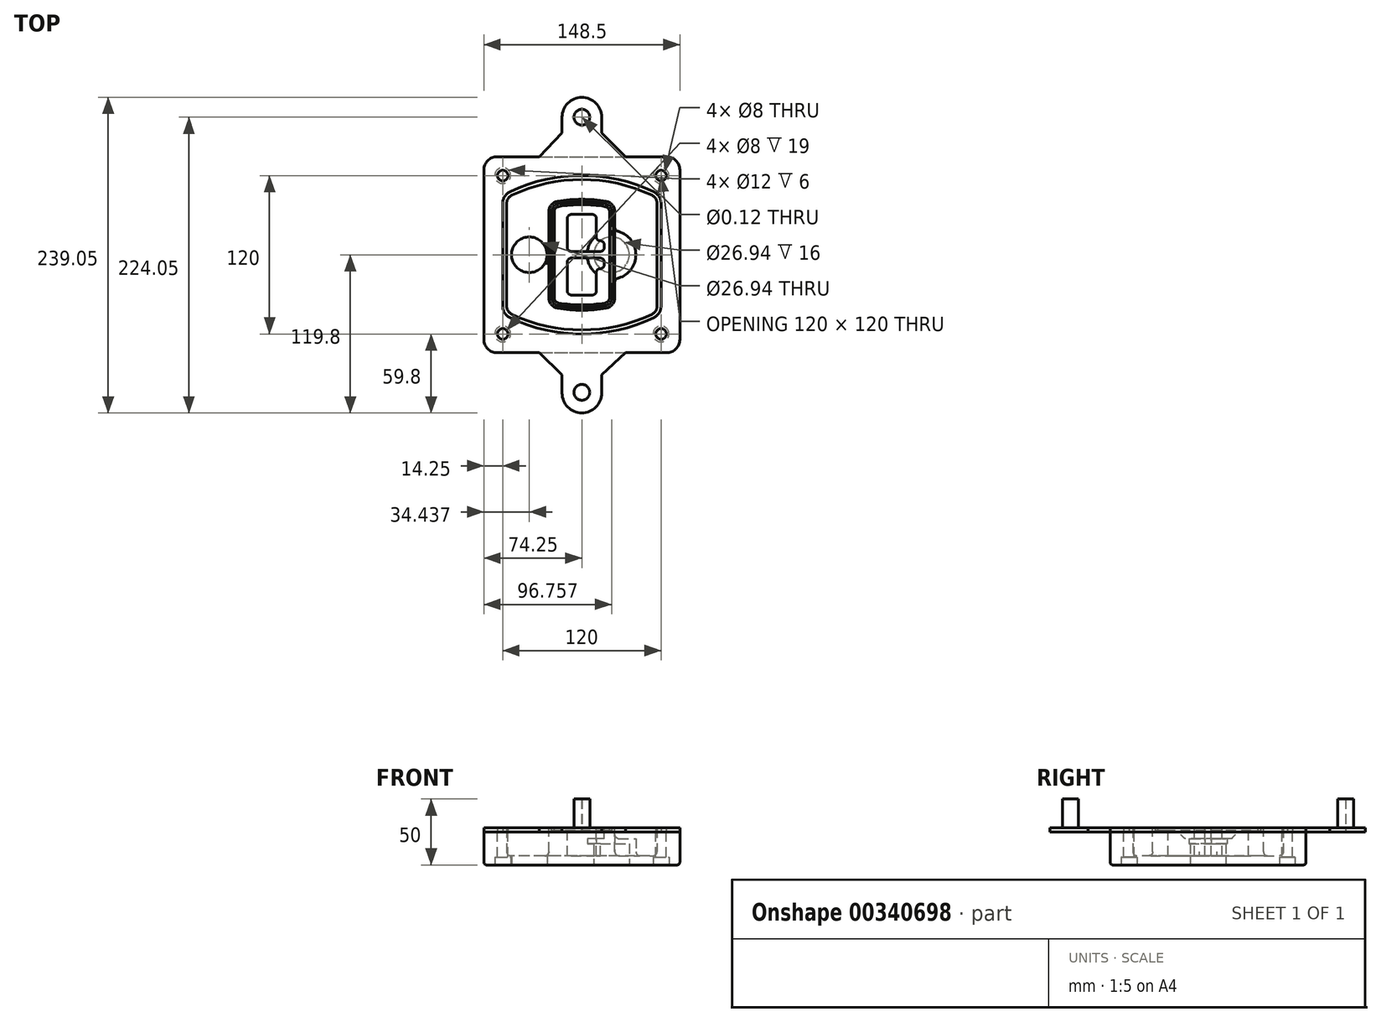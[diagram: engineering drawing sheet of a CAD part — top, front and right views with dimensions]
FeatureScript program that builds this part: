
annotation { "Feature Type Name" : "Feature", "Feature Type Description" : "" }
export const myFeature = defineFeature(function(context is Context, id is Id, definition is map)
    precondition{}
    {
        {
            var Q0;
            Q0=qCreatedBy(makeId("Top.planeOp"),FACE);
            var sketch = newSketch(context, id + "F0", { "sketchPlane" : qUnion([Q0])});
            skPoint(sketch, "E0.rect.middle", {"position": v(0, 0) * mm});
            skLineSegment(sketch, "E1.bottom", {"start": v(-64.25, -74.25) * mm, "end": v(64.25, -74.25) * mm});
            skLineSegment(sketch, "E1.top", {"start": v(-64.25, 74.25) * mm, "end": v(64.25, 74.25) * mm});
            skLineSegment(sketch, "E1.left", {"start": v(-74.25, -64.25) * mm, "end": v(-74.25, 64.25) * mm});
            skLineSegment(sketch, "E1.right", {"start": v(74.25, -64.25) * mm, "end": v(74.25, 64.25) * mm});
            skLineSegment(sketch, "E2", {"start": v(-74.25, 74.25) * mm, "end": v(74.25, -74.25) * mm, "construction": true});
            skLineSegment(sketch, "E3", {"start": v(74.25, 74.25) * mm, "end": v(-74.25, -74.25) * mm, "construction": true});
            skCircle(sketch, "E4", {"center": v(-60, 60) * mm, "radius": 4 * mm});
            skCircle(sketch, "E5", {"center": v(60, 60) * mm, "radius": 4 * mm});
            skCircle(sketch, "E6", {"center": v(60, -60) * mm, "radius": 4 * mm});
            skCircle(sketch, "E7", {"center": v(-60, -60) * mm, "radius": 4 * mm});
            skLineSegment(sketch, "E8", {"start": v(-60, 60) * mm, "end": v(60, 60) * mm, "construction": true});
            skLineSegment(sketch, "E9", {"start": v(60, 60) * mm, "end": v(60, -60) * mm, "construction": true});
            skLineSegment(sketch, "E10", {"start": v(60, -60) * mm, "end": v(-60, -60) * mm, "construction": true});
            skLineSegment(sketch, "E11", {"start": v(-60, -60) * mm, "end": v(-60, 60) * mm, "construction": true});
            skLineSegment(sketch, "E12", {"start": v(-60, 38.83) * mm, "end": v(-60, -38.83) * mm});
            skLineSegment(sketch, "E13", {"start": v(60, 38.83) * mm, "end": v(60, -38.83) * mm});
            skArc(sketch, "E14", {"start": v(54.26, 47.88) * mm, "mid": v(0, 60) * mm, "end": v(-54.26, 47.88) * mm});
            skArc(sketch, "E15", {"start": v(-54.26, -47.88) * mm, "mid": v(0, -60) * mm, "end": v(54.26, -47.88) * mm});
            skLineSegment(sketch, "E16", {"start": v(-60, 0) * mm, "end": v(60, 0) * mm, "construction": true});
            skPoint(sketch, "E17.visualSharp", {"position": v(-60, -45) * mm});
            skArc(sketch, "E17.filletArc", {"start": v(-60, -38.83) * mm, "mid": v(-58.44, -44.2) * mm, "end": v(-54.26, -47.88) * mm});
            skPoint(sketch, "E18.visualSharp", {"position": v(-60, 45) * mm});
            skArc(sketch, "E18.filletArc", {"start": v(-54.26, 47.88) * mm, "mid": v(-58.44, 44.2) * mm, "end": v(-60, 38.83) * mm});
            skPoint(sketch, "E19.visualSharp", {"position": v(60, 45) * mm});
            skArc(sketch, "E19.filletArc", {"start": v(60, 38.83) * mm, "mid": v(58.44, 44.2) * mm, "end": v(54.26, 47.88) * mm});
            skPoint(sketch, "E20.visualSharp", {"position": v(60, -45) * mm});
            skArc(sketch, "E20.filletArc", {"start": v(54.26, -47.88) * mm, "mid": v(58.44, -44.2) * mm, "end": v(60, -38.83) * mm});
            skPoint(sketch, "E21.visualSharp", {"position": v(-74.25, 74.25) * mm});
            skArc(sketch, "E21.filletArc", {"start": v(-64.25, 74.25) * mm, "mid": v(-71.32, 71.32) * mm, "end": v(-74.25, 64.25) * mm});
            skPoint(sketch, "E22.visualSharp", {"position": v(74.25, 74.25) * mm});
            skArc(sketch, "E22.filletArc", {"start": v(74.25, 64.25) * mm, "mid": v(71.32, 71.32) * mm, "end": v(64.25, 74.25) * mm});
            skPoint(sketch, "E23.visualSharp", {"position": v(74.25, -74.25) * mm});
            skArc(sketch, "E23.filletArc", {"start": v(64.25, -74.25) * mm, "mid": v(71.32, -71.32) * mm, "end": v(74.25, -64.25) * mm});
            skPoint(sketch, "E24.visualSharp", {"position": v(-74.25, -74.25) * mm});
            skArc(sketch, "E24.filletArc", {"start": v(-74.25, -64.25) * mm, "mid": v(-71.32, -71.32) * mm, "end": v(-64.25, -74.25) * mm});
            skArc(sketch, "E25.0", {"start": v(57, 38.83) * mm, "mid": v(55.9, 42.58) * mm, "end": v(52.98, 45.17) * mm});
            skLineSegment(sketch, "E25.1", {"start": v(57, 38.83) * mm, "end": v(57, -38.83) * mm});
            skArc(sketch, "E25.2", {"start": v(52.98, -45.17) * mm, "mid": v(55.9, -42.58) * mm, "end": v(57, -38.83) * mm});
            skArc(sketch, "E25.3", {"start": v(-52.98, -45.17) * mm, "mid": v(0, -57) * mm, "end": v(52.98, -45.17) * mm});
            skArc(sketch, "E25.4", {"start": v(-57, -38.83) * mm, "mid": v(-55.9, -42.58) * mm, "end": v(-52.98, -45.17) * mm});
            skArc(sketch, "E25.5", {"start": v(52.98, 45.17) * mm, "mid": v(0, 57) * mm, "end": v(-52.98, 45.17) * mm});
            skLineSegment(sketch, "E25.6", {"start": v(-57, 38.83) * mm, "end": v(-57, -38.83) * mm});
            skArc(sketch, "E25.7", {"start": v(-52.98, 45.17) * mm, "mid": v(-55.9, 42.58) * mm, "end": v(-57, 38.83) * mm});
            skArc(sketch, "E26.0", {"start": v(-55.96, 51.5) * mm, "mid": v(-61.82, 46.33) * mm, "end": v(-64, 38.83) * mm});
            skArc(sketch, "E26.1", {"start": v(55.96, 51.5) * mm, "mid": v(0, 64) * mm, "end": v(-55.96, 51.5) * mm});
            skArc(sketch, "E26.2", {"start": v(64, 38.83) * mm, "mid": v(61.82, 46.33) * mm, "end": v(55.96, 51.5) * mm});
            skLineSegment(sketch, "E26.3", {"start": v(64, 38.83) * mm, "end": v(64, -38.83) * mm});
            skArc(sketch, "E26.4", {"start": v(55.96, -51.5) * mm, "mid": v(61.82, -46.33) * mm, "end": v(64, -38.83) * mm});
            skLineSegment(sketch, "E26.5", {"start": v(-64, 38.83) * mm, "end": v(-64, -38.83) * mm});
            skArc(sketch, "E26.6", {"start": v(-55.96, -51.5) * mm, "mid": v(0, -64) * mm, "end": v(55.96, -51.5) * mm});
            skArc(sketch, "E26.7", {"start": v(-64, -38.83) * mm, "mid": v(-61.82, -46.33) * mm, "end": v(-55.96, -51.5) * mm});
            skSolve(sketch);
        }
        {
            var Q0;
            Q0=makeQuery(id+"F0.imprint","IMPRINT",FACE,{"disambiguationData":[TD([[makeQuery(id+"F0.imprint","IMPRINT",EDGE,{"derivedFrom":sQuery(id+"F0.wireOp",EDGE,"E1.bottom")}),1.0]])]});
            var Q1;
            Q1=makeQuery(id+"F0.imprint","IMPRINT",FACE,{"disambiguationData":[TD([[makeQuery(id+"F0.imprint","IMPRINT",EDGE,{"derivedFrom":sQuery(id+"F0.wireOp",EDGE,"E12")}),1.0]])]});
            var Q2;
            Q2=makeQuery(id+"F0.imprint","IMPRINT",FACE,{"disambiguationData":[TD([[makeQuery(id+"F0.imprint","IMPRINT",EDGE,{"derivedFrom":sQuery(id+"F0.wireOp",EDGE,"E25.0")}),1.0]])]});
            var Q3;
            Q3=makeQuery(id+"F0.imprint","IMPRINT",FACE,{"disambiguationData":[TD([[makeQuery(id+"F0.imprint","IMPRINT",EDGE,{"derivedFrom":sQuery(id+"F0.wireOp",EDGE,"E12")}),-1.0]])]});
            extrude(context, id + "F1", {"entities" : qUnion([Q0, Q1, Q2, Q3]), "oppositeDirection" : true, "depth" : 25 * mm});
        }
        {
            var Q0;
            Q0=makeQuery(id+"F0.imprint","IMPRINT",FACE,{"disambiguationData":[TD([[makeQuery(id+"F0.imprint","IMPRINT",EDGE,{"derivedFrom":sQuery(id+"F0.wireOp",EDGE,"E12")}),1.0]])]});
            extrude(context, id + "F2", {"entities" : qUnion([Q0]), "operationType" : NewBodyOperationType.ADD, "depth" : 3 * mm});
        }
        {
            var Q0;
            Q0=makeQuery(id+"F0.imprint","IMPRINT",FACE,{"disambiguationData":[TD([[makeQuery(id+"F0.imprint","IMPRINT",EDGE,{"derivedFrom":sQuery(id+"F0.wireOp",EDGE,"E25.0")}),1.0]])]});
            extrude(context, id + "F3", {"entities" : qUnion([Q0]), "operationType" : NewBodyOperationType.REMOVE, "oppositeDirection" : true, "depth" : 18 * mm});
        }
        {
            var Q0;
            Q0=makeQuery(id+"F2.opExtrude","CAP_FACE",FACE,{"disambiguationData":[OSD([sQuery(id+"F0.wireOp",EDGE,"E12"),sQuery(id+"F0.wireOp",EDGE,"E13"),sQuery(id+"F0.wireOp",EDGE,"E14"),sQuery(id+"F0.wireOp",EDGE,"E15"),sQuery(id+"F0.wireOp",EDGE,"E17.filletArc"),sQuery(id+"F0.wireOp",EDGE,"E18.filletArc"),sQuery(id+"F0.wireOp",EDGE,"E19.filletArc"),sQuery(id+"F0.wireOp",EDGE,"E20.filletArc"),sQuery(id+"F0.wireOp",EDGE,"E25.0"),sQuery(id+"F0.wireOp",EDGE,"E25.1"),sQuery(id+"F0.wireOp",EDGE,"E25.2"),sQuery(id+"F0.wireOp",EDGE,"E25.3"),sQuery(id+"F0.wireOp",EDGE,"E25.4"),sQuery(id+"F0.wireOp",EDGE,"E25.5"),sQuery(id+"F0.wireOp",EDGE,"E25.6"),sQuery(id+"F0.wireOp",EDGE,"E25.7")])],"isStart":false});
            var sketch = newSketch(context, id + "F4", { "sketchPlane" : qUnion([Q0])});
            skArc(sketch, "E27.0", {"start": v(-18.34, -40.45) * mm, "mid": v(0, -42) * mm, "end": v(18.34, -40.45) * mm});
            skArc(sketch, "E28.0", {"start": v(18.34, 40.45) * mm, "mid": v(0, 42) * mm, "end": v(-18.34, 40.45) * mm});
            skLineSegment(sketch, "E29", {"start": v(-25, 32.57) * mm, "end": v(-25, -32.57) * mm});
            skLineSegment(sketch, "E30", {"start": v(25, 32.57) * mm, "end": v(25, -32.57) * mm});
            skLineSegment(sketch, "E31", {"start": v(-25, 39.1) * mm, "end": v(25, 39.1) * mm, "construction": true});
            skLineSegment(sketch, "E32", {"start": v(-25, -39.1) * mm, "end": v(25, -39.1) * mm, "construction": true});
            skPoint(sketch, "E33.visualSharp", {"position": v(-25, 39.1) * mm});
            skArc(sketch, "E33.filletArc", {"start": v(-18.34, 40.45) * mm, "mid": v(-23.11, 37.73) * mm, "end": v(-25, 32.57) * mm});
            skPoint(sketch, "E34.visualSharp", {"position": v(25, 39.1) * mm});
            skArc(sketch, "E34.filletArc", {"start": v(25, 32.57) * mm, "mid": v(23.11, 37.73) * mm, "end": v(18.34, 40.45) * mm});
            skPoint(sketch, "E35.visualSharp", {"position": v(25, -39.1) * mm});
            skArc(sketch, "E35.filletArc", {"start": v(18.34, -40.45) * mm, "mid": v(23.11, -37.73) * mm, "end": v(25, -32.57) * mm});
            skPoint(sketch, "E36.visualSharp", {"position": v(-25, -39.1) * mm});
            skArc(sketch, "E36.filletArc", {"start": v(-25, -32.57) * mm, "mid": v(-23.11, -37.73) * mm, "end": v(-18.34, -40.45) * mm});
            skArc(sketch, "E37.0", {"start": v(52.98, 45.17) * mm, "mid": v(0, 57) * mm, "end": v(-52.98, 45.17) * mm});
            skArc(sketch, "E37.1", {"start": v(-52.98, 45.17) * mm, "mid": v(-55.9, 42.58) * mm, "end": v(-57, 38.83) * mm});
            skLineSegment(sketch, "E37.2", {"start": v(-57, 38.83) * mm, "end": v(-57, -38.83) * mm});
            skArc(sketch, "E37.3", {"start": v(-57, -38.83) * mm, "mid": v(-55.9, -42.58) * mm, "end": v(-52.98, -45.17) * mm});
            skArc(sketch, "E37.4", {"start": v(-52.98, -45.17) * mm, "mid": v(0, -57) * mm, "end": v(52.98, -45.17) * mm});
            skArc(sketch, "E37.5", {"start": v(52.98, -45.17) * mm, "mid": v(55.9, -42.58) * mm, "end": v(57, -38.83) * mm});
            skLineSegment(sketch, "E37.6", {"start": v(57, 38.83) * mm, "end": v(57, -38.83) * mm});
            skArc(sketch, "E37.7", {"start": v(57, 38.83) * mm, "mid": v(55.9, 42.58) * mm, "end": v(52.98, 45.17) * mm});
            skLineSegment(sketch, "E38.0", {"start": v(23, 32.57) * mm, "end": v(23, -32.57) * mm});
            skArc(sketch, "E38.1", {"start": v(18, -38.48) * mm, "mid": v(21.58, -36.44) * mm, "end": v(23, -32.57) * mm});
            skArc(sketch, "E38.2", {"start": v(-18, -38.48) * mm, "mid": v(0, -40) * mm, "end": v(18, -38.48) * mm});
            skArc(sketch, "E38.3", {"start": v(-23, -32.57) * mm, "mid": v(-21.58, -36.44) * mm, "end": v(-18, -38.48) * mm});
            skLineSegment(sketch, "E38.4", {"start": v(-23, 32.57) * mm, "end": v(-23, -32.57) * mm});
            skArc(sketch, "E38.5", {"start": v(23, 32.57) * mm, "mid": v(21.58, 36.44) * mm, "end": v(18, 38.48) * mm});
            skArc(sketch, "E38.6", {"start": v(-18, 38.48) * mm, "mid": v(-21.58, 36.44) * mm, "end": v(-23, 32.57) * mm});
            skArc(sketch, "E38.7", {"start": v(18, 38.48) * mm, "mid": v(0, 40) * mm, "end": v(-18, 38.48) * mm});
            skArc(sketch, "E39.0", {"start": v(21, 32.57) * mm, "mid": v(20.06, 35.15) * mm, "end": v(17.67, 36.5) * mm});
            skLineSegment(sketch, "E39.1", {"start": v(21, 32.57) * mm, "end": v(21, -32.57) * mm});
            skArc(sketch, "E39.2", {"start": v(17.67, -36.5) * mm, "mid": v(20.06, -35.15) * mm, "end": v(21, -32.57) * mm});
            skArc(sketch, "E39.3", {"start": v(-17.67, -36.5) * mm, "mid": v(0, -38) * mm, "end": v(17.67, -36.5) * mm});
            skArc(sketch, "E39.4", {"start": v(-21, -32.57) * mm, "mid": v(-20.06, -35.15) * mm, "end": v(-17.67, -36.5) * mm});
            skArc(sketch, "E39.5", {"start": v(17.67, 36.5) * mm, "mid": v(0, 38) * mm, "end": v(-17.67, 36.5) * mm});
            skLineSegment(sketch, "E39.6", {"start": v(-21, 32.57) * mm, "end": v(-21, -32.57) * mm});
            skArc(sketch, "E39.7", {"start": v(-17.67, 36.5) * mm, "mid": v(-20.06, 35.15) * mm, "end": v(-21, 32.57) * mm});
            skLineSegment(sketch, "E40", {"start": v(-25, 0) * mm, "end": v(25, 0) * mm, "construction": true});
            skLineSegment(sketch, "E41", {"start": v(-11, 5.5) * mm, "end": v(-11, 27.5) * mm});
            skLineSegment(sketch, "E42", {"start": v(-8, 30.5) * mm, "end": v(8, 30.5) * mm});
            skLineSegment(sketch, "E43", {"start": v(11, 27.5) * mm, "end": v(11, 13.5) * mm});
            skLineSegment(sketch, "E44", {"start": v(14, 10.5) * mm, "end": v(14, 10.5) * mm});
            skLineSegment(sketch, "E45", {"start": v(17, 7.5) * mm, "end": v(17, 5.5) * mm});
            skLineSegment(sketch, "E46", {"start": v(14, 2.5) * mm, "end": v(-8, 2.5) * mm});
            skPoint(sketch, "E47.visualSharp", {"position": v(-11, 30.5) * mm});
            skArc(sketch, "E47.filletArc", {"start": v(-8, 30.5) * mm, "mid": v(-10.12, 29.62) * mm, "end": v(-11, 27.5) * mm});
            skPoint(sketch, "E48.visualSharp", {"position": v(11, 30.5) * mm});
            skArc(sketch, "E48.filletArc", {"start": v(11, 27.5) * mm, "mid": v(10.12, 29.62) * mm, "end": v(8, 30.5) * mm});
            skPoint(sketch, "E49.visualSharp", {"position": v(11, 10.5) * mm});
            skArc(sketch, "E49.filletArc", {"start": v(11, 13.5) * mm, "mid": v(11.88, 11.38) * mm, "end": v(14, 10.5) * mm});
            skPoint(sketch, "E50.visualSharp", {"position": v(17, 10.5) * mm});
            skArc(sketch, "E50.filletArc", {"start": v(17, 7.5) * mm, "mid": v(16.12, 9.62) * mm, "end": v(14, 10.5) * mm});
            skPoint(sketch, "E51.visualSharp", {"position": v(17, 2.5) * mm});
            skArc(sketch, "E51.filletArc", {"start": v(14, 2.5) * mm, "mid": v(16.12, 3.38) * mm, "end": v(17, 5.5) * mm});
            skPoint(sketch, "E52.visualSharp", {"position": v(-11, 2.5) * mm});
            skArc(sketch, "E52.filletArc", {"start": v(-11, 5.5) * mm, "mid": v(-10.12, 3.38) * mm, "end": v(-8, 2.5) * mm});
            skLineSegment(sketch, "E53.0.MirrorCS", {"start": v(14, -2.5) * mm, "end": v(-8, -2.5) * mm});
            skArc(sketch, "E54.0.MirrorCS", {"start": v(-11, -5.5) * mm, "mid": v(-10.12, -3.38) * mm, "end": v(-8, -2.5) * mm});
            skLineSegment(sketch, "E55.0.MirrorCS", {"start": v(-11, -5.5) * mm, "end": v(-11, -27.5) * mm});
            skArc(sketch, "E56.0.MirrorCS", {"start": v(-8, -30.5) * mm, "mid": v(-10.12, -29.62) * mm, "end": v(-11, -27.5) * mm});
            skLineSegment(sketch, "E57.0.MirrorCS", {"start": v(-8, -30.5) * mm, "end": v(8, -30.5) * mm});
            skArc(sketch, "E58.0.MirrorCS", {"start": v(11, -27.5) * mm, "mid": v(10.12, -29.62) * mm, "end": v(8, -30.5) * mm});
            skLineSegment(sketch, "E59.0.MirrorCS", {"start": v(11, -27.5) * mm, "end": v(11, -13.5) * mm});
            skArc(sketch, "E60.0.MirrorCS", {"start": v(11, -13.5) * mm, "mid": v(11.88, -11.38) * mm, "end": v(14, -10.5) * mm});
            skArc(sketch, "E61.0.MirrorCS", {"start": v(17, -7.5) * mm, "mid": v(16.12, -9.62) * mm, "end": v(14, -10.5) * mm});
            skLineSegment(sketch, "E62.0.MirrorCS", {"start": v(17, -7.5) * mm, "end": v(17, -5.5) * mm});
            skArc(sketch, "E63.0.MirrorCS", {"start": v(14, -2.5) * mm, "mid": v(16.12, -3.38) * mm, "end": v(17, -5.5) * mm});
            skSolve(sketch);
        }
        {
            var Q0;
            Q0=makeQuery(id+"F4.imprint","IMPRINT",FACE,{"disambiguationData":[TD([[makeQuery(id+"F4.imprint","IMPRINT",EDGE,{"derivedFrom":sQuery(id+"F4.wireOp",EDGE,"E27.0")}),1.0]])]});
            var Q1;
            Q1=makeQuery(id+"F4.imprint","IMPRINT",FACE,{"disambiguationData":[TD([[makeQuery(id+"F4.imprint","IMPRINT",EDGE,{"derivedFrom":sQuery(id+"F4.wireOp",EDGE,"E38.0")}),-1.0]])]});
            var Q2;
            Q2=makeQuery(id+"F4.imprint","IMPRINT",FACE,{"disambiguationData":[TD([[makeQuery(id+"F4.imprint","IMPRINT",EDGE,{"derivedFrom":sQuery(id+"F4.wireOp",EDGE,"E39.0")}),1.0]])]});
            extrude(context, id + "F5", {"entities" : qUnion([Q0, Q1, Q2]), "operationType" : NewBodyOperationType.ADD, "endBound" : BoundingType.UP_TO_NEXT, "oppositeDirection" : true, "depth" : 25 * mm});
        }
        {
            var Q0;
            Q0=makeQuery(id+"F4.imprint","IMPRINT",FACE,{"disambiguationData":[TD([[makeQuery(id+"F4.imprint","IMPRINT",EDGE,{"derivedFrom":sQuery(id+"F4.wireOp",EDGE,"E38.0")}),-1.0]])]});
            extrude(context, id + "F6", {"entities" : qUnion([Q0]), "operationType" : NewBodyOperationType.REMOVE, "oppositeDirection" : true, "depth" : 2 * mm});
        }
        {
            var Q0;
            Q0=makeQuery(id+"F1.opExtrude","CAP_FACE",FACE,{"disambiguationData":[OSD([sQuery(id+"F0.wireOp",EDGE,"E1.bottom"),sQuery(id+"F0.wireOp",EDGE,"E1.top"),sQuery(id+"F0.wireOp",EDGE,"E1.left"),sQuery(id+"F0.wireOp",EDGE,"E1.right"),sQuery(id+"F0.wireOp",EDGE,"E4"),sQuery(id+"F0.wireOp",EDGE,"E5"),sQuery(id+"F0.wireOp",EDGE,"E6"),sQuery(id+"F0.wireOp",EDGE,"E7"),sQuery(id+"F0.wireOp",EDGE,"E21.filletArc"),sQuery(id+"F0.wireOp",EDGE,"E22.filletArc"),sQuery(id+"F0.wireOp",EDGE,"E23.filletArc"),sQuery(id+"F0.wireOp",EDGE,"E24.filletArc")])],"isStart":false});
            var sketch = newSketch(context, id + "F7", { "sketchPlane" : qUnion([Q0])});
            skCircle(sketch, "E64", {"center": v(22.5, 0) * mm, "radius": 13.47 * mm});
            skCircle(sketch, "E65", {"center": v(-39.81, 0) * mm, "radius": 13.47 * mm});
            skLineSegment(sketch, "E66", {"start": v(74.25, 0) * mm, "end": v(-74.25, 0) * mm});
            skCircle(sketch, "E67", {"center": v(22.5, 0) * mm, "radius": 18.47 * mm});
            skCircle(sketch, "E68", {"center": v(60, -60) * mm, "radius": 6 * mm});
            skCircle(sketch, "E69", {"center": v(-60, -60) * mm, "radius": 6 * mm});
            skCircle(sketch, "E70", {"center": v(-60, 60) * mm, "radius": 6 * mm});
            skCircle(sketch, "E71", {"center": v(60, 60) * mm, "radius": 6 * mm});
            skSolve(sketch);
        }
        {
            var Q0;
            {var subQ1=sQuery(id+"F7.wireOp",EDGE,"E66");var subQ4=sQuery(id+"F7.wireOp",EDGE,"E64");var subQ6=makeQuery(id+"F7.imprint","INTERSECT",VERTEX,{"disambiguationData":[OD(0.0)],"derivedFrom":[subQ4,subQ1]});Q0=makeQuery(id+"F7.imprint","IMPRINT",FACE,{"disambiguationData":[TD([[makeQuery(id+"F7.imprint","IMPRINT",EDGE,{"disambiguationData":[TD([[subQ6,-1.0]])],"derivedFrom":subQ4}),-1.0]])]});}
            var Q1;
            {var subQ0=sQuery(id+"F7.wireOp",EDGE,"E66");var subQ1=sQuery(id+"F7.wireOp",EDGE,"E64");var subQ3=makeQuery(id+"F7.imprint","INTERSECT",VERTEX,{"disambiguationData":[OD(0.0)],"derivedFrom":[subQ1,subQ0]});Q1=makeQuery(id+"F7.imprint","IMPRINT",FACE,{"disambiguationData":[TD([[makeQuery(id+"F7.imprint","IMPRINT",EDGE,{"disambiguationData":[TD([[subQ3,-1.0]])],"derivedFrom":subQ1}),1.0]])]});}
            var Q2;
            {var subQ0=sQuery(id+"F7.wireOp",EDGE,"E66");var subQ1=sQuery(id+"F7.wireOp",EDGE,"E64");var subQ3=makeQuery(id+"F7.imprint","INTERSECT",VERTEX,{"disambiguationData":[OD(0.0)],"derivedFrom":[subQ1,subQ0]});Q2=makeQuery(id+"F7.imprint","IMPRINT",FACE,{"disambiguationData":[TD([[makeQuery(id+"F7.imprint","IMPRINT",EDGE,{"disambiguationData":[TD([[subQ3,1.0]])],"derivedFrom":subQ1}),1.0]])]});}
            var Q3;
            {var subQ1=sQuery(id+"F7.wireOp",EDGE,"E66");var subQ4=sQuery(id+"F7.wireOp",EDGE,"E64");var subQ6=makeQuery(id+"F7.imprint","INTERSECT",VERTEX,{"disambiguationData":[OD(0.0)],"derivedFrom":[subQ4,subQ1]});Q3=makeQuery(id+"F7.imprint","IMPRINT",FACE,{"disambiguationData":[TD([[makeQuery(id+"F7.imprint","IMPRINT",EDGE,{"disambiguationData":[TD([[subQ6,1.0]])],"derivedFrom":subQ4}),-1.0]])]});}
            extrude(context, id + "F8", {"entities" : qUnion([Q0, Q1, Q2, Q3]), "operationType" : NewBodyOperationType.ADD, "oppositeDirection" : true, "depth" : 20 * mm});
        }
        {
            var Q0;
            {var subQ0=sQuery(id+"F7.wireOp",EDGE,"E66");var subQ1=sQuery(id+"F7.wireOp",EDGE,"E64");var subQ3=makeQuery(id+"F7.imprint","INTERSECT",VERTEX,{"disambiguationData":[OD(0.0)],"derivedFrom":[subQ1,subQ0]});Q0=makeQuery(id+"F7.imprint","IMPRINT",FACE,{"disambiguationData":[TD([[makeQuery(id+"F7.imprint","IMPRINT",EDGE,{"disambiguationData":[TD([[subQ3,-1.0]])],"derivedFrom":subQ1}),1.0]])]});}
            var Q1;
            {var subQ0=sQuery(id+"F7.wireOp",EDGE,"E66");var subQ1=sQuery(id+"F7.wireOp",EDGE,"E64");var subQ3=makeQuery(id+"F7.imprint","INTERSECT",VERTEX,{"disambiguationData":[OD(0.0)],"derivedFrom":[subQ1,subQ0]});Q1=makeQuery(id+"F7.imprint","IMPRINT",FACE,{"disambiguationData":[TD([[makeQuery(id+"F7.imprint","IMPRINT",EDGE,{"disambiguationData":[TD([[subQ3,1.0]])],"derivedFrom":subQ1}),1.0]])]});}
            extrude(context, id + "F9", {"entities" : qUnion([Q0, Q1]), "operationType" : NewBodyOperationType.REMOVE, "oppositeDirection" : true, "depth" : 16 * mm});
        }
        {
            var Q0;
            {var subQ0=sQuery(id+"F7.wireOp",EDGE,"E66");var subQ1=sQuery(id+"F7.wireOp",EDGE,"E65");var subQ3=makeQuery(id+"F7.imprint","INTERSECT",VERTEX,{"disambiguationData":[OD(0.0)],"derivedFrom":[subQ1,subQ0]});Q0=makeQuery(id+"F7.imprint","IMPRINT",FACE,{"disambiguationData":[TD([[makeQuery(id+"F7.imprint","IMPRINT",EDGE,{"disambiguationData":[TD([[subQ3,-1.0]])],"derivedFrom":subQ1}),1.0]])]});}
            var Q1;
            {var subQ0=sQuery(id+"F7.wireOp",EDGE,"E66");var subQ1=sQuery(id+"F7.wireOp",EDGE,"E65");var subQ3=makeQuery(id+"F7.imprint","INTERSECT",VERTEX,{"disambiguationData":[OD(0.0)],"derivedFrom":[subQ1,subQ0]});Q1=makeQuery(id+"F7.imprint","IMPRINT",FACE,{"disambiguationData":[TD([[makeQuery(id+"F7.imprint","IMPRINT",EDGE,{"disambiguationData":[TD([[subQ3,1.0]])],"derivedFrom":subQ1}),1.0]])]});}
            extrude(context, id + "F10", {"entities" : qUnion([Q0, Q1]), "operationType" : NewBodyOperationType.REMOVE, "oppositeDirection" : true, "depth" : 25 * mm});
        }
        {
            var Q0;
            Q0=makeQuery(id+"F7.imprint","IMPRINT",FACE,{"disambiguationData":[TD([[makeQuery(id+"F7.imprint","IMPRINT",EDGE,{"derivedFrom":sQuery(id+"F7.wireOp",EDGE,"E68")}),1.0]])]});
            var Q1;
            Q1=makeQuery(id+"F7.imprint","IMPRINT",FACE,{"disambiguationData":[TD([[makeQuery(id+"F7.imprint","IMPRINT",EDGE,{"derivedFrom":makeQuery(id+"F1.opExtrude","CAP_EDGE",EDGE,{"disambiguationData":[OSD([sQuery(id+"F0.wireOp",EDGE,"E5")])],"isStart":false})}),-1.0]])]});
            var Q2;
            Q2=makeQuery(id+"F7.imprint","IMPRINT",FACE,{"disambiguationData":[TD([[makeQuery(id+"F7.imprint","IMPRINT",EDGE,{"derivedFrom":sQuery(id+"F7.wireOp",EDGE,"E69")}),1.0]])]});
            var Q3;
            Q3=makeQuery(id+"F7.imprint","IMPRINT",FACE,{"disambiguationData":[TD([[makeQuery(id+"F7.imprint","IMPRINT",EDGE,{"derivedFrom":makeQuery(id+"F1.opExtrude","CAP_EDGE",EDGE,{"disambiguationData":[OSD([sQuery(id+"F0.wireOp",EDGE,"E4")])],"isStart":false})}),-1.0]])]});
            var Q4;
            Q4=makeQuery(id+"F7.imprint","IMPRINT",FACE,{"disambiguationData":[TD([[makeQuery(id+"F7.imprint","IMPRINT",EDGE,{"derivedFrom":sQuery(id+"F7.wireOp",EDGE,"E70")}),1.0]])]});
            var Q5;
            Q5=makeQuery(id+"F7.imprint","IMPRINT",FACE,{"disambiguationData":[TD([[makeQuery(id+"F7.imprint","IMPRINT",EDGE,{"derivedFrom":makeQuery(id+"F1.opExtrude","CAP_EDGE",EDGE,{"disambiguationData":[OSD([sQuery(id+"F0.wireOp",EDGE,"E7")])],"isStart":false})}),-1.0]])]});
            var Q6;
            Q6=makeQuery(id+"F7.imprint","IMPRINT",FACE,{"disambiguationData":[TD([[makeQuery(id+"F7.imprint","IMPRINT",EDGE,{"derivedFrom":sQuery(id+"F7.wireOp",EDGE,"E71")}),1.0]])]});
            var Q7;
            Q7=makeQuery(id+"F7.imprint","IMPRINT",FACE,{"disambiguationData":[TD([[makeQuery(id+"F7.imprint","IMPRINT",EDGE,{"derivedFrom":makeQuery(id+"F1.opExtrude","CAP_EDGE",EDGE,{"disambiguationData":[OSD([sQuery(id+"F0.wireOp",EDGE,"E6")])],"isStart":false})}),-1.0]])]});
            extrude(context, id + "F11", {"entities" : qUnion([Q0, Q1, Q2, Q3, Q4, Q5, Q6, Q7]), "operationType" : NewBodyOperationType.REMOVE, "oppositeDirection" : true, "depth" : 6 * mm});
        }
        {
            var Q0;
            Q0=makeQuery(id+"F9.boolean.opBoolean","COPY",FACE,{"derivedFrom":makeQuery(id+"F9.opExtrude","CAP_FACE",FACE,{"disambiguationData":[OSD([sQuery(id+"F7.wireOp",EDGE,"E64")])],"isStart":false})});
            var sketch = newSketch(context, id + "F12", { "sketchPlane" : qUnion([Q0])});
            skArc(sketch, "E72.0", {"start": v(11, 14.45) * mm, "mid": v(6.45, 9.13) * mm, "end": v(4.2, 2.5) * mm});
            skArc(sketch, "E72.1", {"start": v(4.2, -2.5) * mm, "mid": v(6.45, -9.13) * mm, "end": v(11, -14.45) * mm});
            skLineSegment(sketch, "E73", {"start": v(4.2, -2.5) * mm, "end": v(14, -2.5) * mm});
            skLineSegment(sketch, "E74.0", {"start": v(14, 2.5) * mm, "end": v(4.2, 2.5) * mm});
            skArc(sketch, "E74.1", {"start": v(14, 2.5) * mm, "mid": v(16.12, 3.38) * mm, "end": v(17, 5.5) * mm});
            skLineSegment(sketch, "E74.2", {"start": v(17, 7.5) * mm, "end": v(17, 5.5) * mm});
            skArc(sketch, "E74.3", {"start": v(17, 7.5) * mm, "mid": v(16.12, 9.62) * mm, "end": v(14, 10.5) * mm});
            skArc(sketch, "E74.4", {"start": v(11, 13.5) * mm, "mid": v(11.88, 11.38) * mm, "end": v(14, 10.5) * mm});
            skLineSegment(sketch, "E74.5", {"start": v(11, 14.45) * mm, "end": v(11, 13.5) * mm});
            skLineSegment(sketch, "E74.7", {"start": v(14, -2.5) * mm, "end": v(4.2, -2.5) * mm});
            skArc(sketch, "E74.8", {"start": v(14, -2.5) * mm, "mid": v(16.12, -3.38) * mm, "end": v(17, -5.5) * mm});
            skLineSegment(sketch, "E74.9", {"start": v(17, -7.5) * mm, "end": v(17, -5.5) * mm});
            skArc(sketch, "E74.10", {"start": v(17, -7.5) * mm, "mid": v(16.12, -9.62) * mm, "end": v(14, -10.5) * mm});
            skArc(sketch, "E74.11", {"start": v(11, -13.5) * mm, "mid": v(11.88, -11.38) * mm, "end": v(14, -10.5) * mm});
            skLineSegment(sketch, "E74.12", {"start": v(11, -14.45) * mm, "end": v(11, -13.5) * mm});
            skPoint(sketch, "E75.orphan", {"position": v(11, -27.5) * mm});
            skPoint(sketch, "E76.orphan", {"position": v(-8, -2.5) * mm});
            skPoint(sketch, "E77.orphan", {"position": v(-8, 2.5) * mm});
            skPoint(sketch, "E78.orphan", {"position": v(11, 27.5) * mm});
            skSolve(sketch);
        }
        {
            var Q0;
            {var subQ7=sQuery(id+"F12.wireOp",EDGE,"E72.0");var subQ14=sQuery(id+"F12.wireOp",EDGE,"E72.1");var subQ16=sQuery(id+"F12.wireOp",EDGE,"E74.1");var subQ18=sQuery(id+"F12.wireOp",EDGE,"E74.8");Q0=qUnion([makeQuery(id+"F12.imprint","IMPRINT",FACE,{"disambiguationData":[TD([[makeQuery(id+"F12.imprint","IMPRINT",EDGE,{"derivedFrom":subQ7}),1.0]])]}),makeQuery(id+"F12.imprint","IMPRINT",FACE,{"disambiguationData":[TD([[makeQuery(id+"F12.imprint","IMPRINT",EDGE,{"derivedFrom":subQ14}),1.0]])]}),makeQuery(id+"F12.imprint","IMPRINT",FACE,{"disambiguationData":[TD([[makeQuery(id+"F12.imprint","IMPRINT",EDGE,{"derivedFrom":subQ16}),1.0]])]}),makeQuery(id+"F12.imprint","IMPRINT",FACE,{"disambiguationData":[TD([[makeQuery(id+"F12.imprint","IMPRINT",EDGE,{"derivedFrom":subQ18}),-1.0]])]})]);}
            var Q1;
            Q1=makeQuery(id+"F5.boolean.opBoolean","SPLIT",FACE,{"disambiguationData":[TD([makeQuery(id+"F5.opExtrude","SWEPT_FACE",FACE,{"disambiguationData":[OSD([sQuery(id+"F4.wireOp",EDGE,"E41")])]})])],"derivedFrom":makeQuery(id+"F3.boolean.opBoolean","COPY",FACE,{"derivedFrom":makeQuery(id+"F3.opExtrude","CAP_FACE",FACE,{"disambiguationData":[OSD([sQuery(id+"F0.wireOp",EDGE,"E25.0"),sQuery(id+"F0.wireOp",EDGE,"E25.1"),sQuery(id+"F0.wireOp",EDGE,"E25.2"),sQuery(id+"F0.wireOp",EDGE,"E25.3"),sQuery(id+"F0.wireOp",EDGE,"E25.4"),sQuery(id+"F0.wireOp",EDGE,"E25.5"),sQuery(id+"F0.wireOp",EDGE,"E25.6"),sQuery(id+"F0.wireOp",EDGE,"E25.7")])],"isStart":false})})});
            extrude(context, id + "F13", {"entities" : qUnion([Q0]), "operationType" : NewBodyOperationType.REMOVE, "endBound" : BoundingType.UP_TO_SURFACE, "endBoundEntityFace" : qUnion([Q1]), "depth" : 25 * mm});
        }
        {
            var Q0;
            Q0=makeQuery(id+"F3.boolean.opBoolean","COPY",EDGE,{"derivedFrom":makeQuery(id+"F3.opExtrude","CAP_EDGE",EDGE,{"disambiguationData":[OSD([sQuery(id+"F0.wireOp",EDGE,"E25.6")])],"isStart":false})});
            var Q1;
            Q1=makeQuery(id+"F8.boolean.opBoolean","INTERSECT",EDGE,{"derivedFrom":[makeQuery(id+"F5.opExtrude","SWEPT_FACE",FACE,{"disambiguationData":[OSD([sQuery(id+"F4.wireOp",EDGE,"E30")])]}),makeQuery(id+"F8.opExtrude","CAP_FACE",FACE,{"disambiguationData":[OSD([sQuery(id+"F7.wireOp",EDGE,"E67")])],"isStart":false})]});
            var Q2;
            Q2=makeQuery(id+"F8.boolean.opBoolean","INTERSECT",EDGE,{"disambiguationData":[OD(1.0)],"derivedFrom":[makeQuery(id+"F5.opExtrude","SWEPT_FACE",FACE,{"disambiguationData":[OSD([sQuery(id+"F4.wireOp",EDGE,"E30")])]}),makeQuery(id+"F8.opExtrude","SWEPT_FACE",FACE,{"disambiguationData":[OSD([sQuery(id+"F7.wireOp",EDGE,"E67")])]})]});
            var Q3;
            {var subQ0=sQuery(id+"F4.wireOp",EDGE,"E30");Q3=makeQuery(id+"F8.boolean.opBoolean","SPLIT",EDGE,{"disambiguationData":[TD([makeQuery(id+"F5.opExtrude","SWEPT_FACE",FACE,{"disambiguationData":[OSD([sQuery(id+"F4.wireOp",EDGE,"E35.filletArc")])]})])],"derivedFrom":makeQuery(id+"F5.opExtrude","CAP_EDGE",EDGE,{"disambiguationData":[OSD([subQ0])],"isStart":false})});}
            var Q4;
            {var subQ0=sQuery(id+"F0.wireOp",EDGE,"E25.7");var subQ1=sQuery(id+"F0.wireOp",EDGE,"E25.1");var subQ2=sQuery(id+"F0.wireOp",EDGE,"E25.6");var subQ3=sQuery(id+"F0.wireOp",EDGE,"E25.5");var subQ4=sQuery(id+"F0.wireOp",EDGE,"E25.4");var subQ5=sQuery(id+"F0.wireOp",EDGE,"E25.0");var subQ6=sQuery(id+"F0.wireOp",EDGE,"E25.2");var subQ7=sQuery(id+"F0.wireOp",EDGE,"E25.3");Q4=makeQuery(id+"F8.boolean.opBoolean","INTERSECT",EDGE,{"derivedFrom":[makeQuery(id+"F5.boolean.opBoolean","SPLIT",FACE,{"disambiguationData":[TD([makeQuery(id+"F2.opExtrude","SWEPT_FACE",FACE,{"disambiguationData":[OSD([subQ5])]})])],"derivedFrom":makeQuery(id+"F3.boolean.opBoolean","COPY",FACE,{"derivedFrom":makeQuery(id+"F3.opExtrude","CAP_FACE",FACE,{"disambiguationData":[OSD([subQ5,subQ1,subQ6,subQ7,subQ4,subQ3,subQ2,subQ0])],"isStart":false})})}),makeQuery(id+"F8.opExtrude","SWEPT_FACE",FACE,{"disambiguationData":[OSD([sQuery(id+"F7.wireOp",EDGE,"E67")])]})]});}
            var Q5;
            Q5=makeQuery(id+"F8.boolean.opBoolean","INTERSECT",EDGE,{"disambiguationData":[OD(0.0)],"derivedFrom":[makeQuery(id+"F5.opExtrude","SWEPT_FACE",FACE,{"disambiguationData":[OSD([sQuery(id+"F4.wireOp",EDGE,"E30")])]}),makeQuery(id+"F8.opExtrude","SWEPT_FACE",FACE,{"disambiguationData":[OSD([sQuery(id+"F7.wireOp",EDGE,"E67")])]})]});
            fillet(context, id + "F14", {"entities" : qUnion([Q0, Q1, Q2, Q3, Q4, Q5]), "radius" : 3 * mm, "tangentPropagation" : true, "allowEdgeOverflow" : false});
        }
        {
            var Q0;
            Q0=makeQuery(id+"F1.opExtrude","CAP_EDGE",EDGE,{"disambiguationData":[OSD([sQuery(id+"F0.wireOp",EDGE,"E1.bottom")])],"isStart":false});
            fillet(context, id + "F15", {"entities" : qUnion([Q0]), "radius" : 2 * mm, "tangentPropagation" : true, "allowEdgeOverflow" : false});
        }
        {
            var Q0;
            {var subQ0=sQuery(id+"F0.wireOp",EDGE,"E21.filletArc");var subQ1=sQuery(id+"F0.wireOp",EDGE,"E7");var subQ2=sQuery(id+"F0.wireOp",EDGE,"E6");var subQ3=sQuery(id+"F0.wireOp",EDGE,"E5");var subQ4=sQuery(id+"F0.wireOp",EDGE,"E4");var subQ5=sQuery(id+"F0.wireOp",EDGE,"E22.filletArc");var subQ6=sQuery(id+"F0.wireOp",EDGE,"E1.bottom");var subQ7=sQuery(id+"F0.wireOp",EDGE,"E1.right");var subQ8=sQuery(id+"F0.wireOp",EDGE,"E1.top");var subQ9=sQuery(id+"F0.wireOp",EDGE,"E1.left");var subQ10=sQuery(id+"F0.wireOp",EDGE,"E23.filletArc");var subQ11=sQuery(id+"F0.wireOp",EDGE,"E24.filletArc");Q0=makeQuery(id+"F2.boolean.opBoolean","SPLIT",FACE,{"disambiguationData":[TD([makeQuery(id+"F1.opExtrude","SWEPT_FACE",FACE,{"disambiguationData":[OSD([subQ6])]})])],"derivedFrom":makeQuery(id+"F1.opExtrude","CAP_FACE",FACE,{"disambiguationData":[OSD([subQ6,subQ8,subQ9,subQ7,subQ4,subQ3,subQ2,subQ1,subQ0,subQ5,subQ10,subQ11])],"isStart":true})});}
            var sketch = newSketch(context, id + "F16", { "sketchPlane" : qUnion([Q0])});
            skCircle(sketch, "E79", {"center": v(0, 104.25) * mm, "radius": 0.06 * mm});
            skLineSegment(sketch, "E80", {"start": v(0, 74.25) * mm, "end": v(0, 104.25) * mm, "construction": true});
            skCircle(sketch, "E81", {"center": v(0, 104.25) * mm, "radius": 6 * mm});
            skLineSegment(sketch, "E82", {"start": v(-32.35, 74.25) * mm, "end": v(-15, 92.25) * mm});
            skLineSegment(sketch, "E83", {"start": v(33, 74.25) * mm, "end": v(15, 92.25) * mm});
            skLineSegment(sketch, "E84", {"start": v(15, 92.25) * mm, "end": v(15, 104.25) * mm});
            skLineSegment(sketch, "E85", {"start": v(-15, 92.25) * mm, "end": v(-15, 104.25) * mm});
            skArc(sketch, "E86", {"start": v(15, 104.25) * mm, "mid": v(0, 119.25) * mm, "end": v(-15, 104.25) * mm});
            skLineSegment(sketch, "E87", {"start": v(-32.35, -74.25) * mm, "end": v(-15, -90.97) * mm});
            skLineSegment(sketch, "E88", {"start": v(0, -74.25) * mm, "end": v(0, -104.25) * mm, "construction": true});
            skLineSegment(sketch, "E89", {"start": v(-15, -90.97) * mm, "end": v(-15, -104.8) * mm});
            skLineSegment(sketch, "E90", {"start": v(33, -74.25) * mm, "end": v(15, -90.97) * mm});
            skLineSegment(sketch, "E91", {"start": v(15, -90.97) * mm, "end": v(15, -104.8) * mm});
            skCircle(sketch, "E92", {"center": v(0, -104.25) * mm, "radius": 6 * mm});
            skArc(sketch, "E93", {"start": v(-15, -104.8) * mm, "mid": v(0, -119.8) * mm, "end": v(15, -104.8) * mm});
            skSolve(sketch);
        }
        {
            var Q0;
            Q0=makeQuery(id+"F16.imprint","IMPRINT",FACE,{"disambiguationData":[TD([[makeQuery(id+"F16.imprint","IMPRINT",EDGE,{"derivedFrom":makeQuery(id+"F1.opExtrude","CAP_EDGE",EDGE,{"disambiguationData":[OSD([sQuery(id+"F0.wireOp",EDGE,"E1.left")])],"isStart":true})}),-1.0]])]});
            var Q1;
            Q1=makeQuery(id+"F16.imprint","IMPRINT",FACE,{"disambiguationData":[TD([[makeQuery(id+"F16.imprint","IMPRINT",EDGE,{"derivedFrom":sQuery(id+"F16.wireOp",EDGE,"E81")}),-1.0]])]});
            var Q2;
            {var subQ1=sQuery(id+"F16.wireOp",EDGE,"E87");Q2=makeQuery(id+"F16.imprint","IMPRINT",FACE,{"disambiguationData":[TD([[makeQuery(id+"F16.imprint","IMPRINT",EDGE,{"derivedFrom":subQ1}),1.0]])]});}
            var Q3;
            Q3=makeQuery(id+"F2.opExtrude","CAP_FACE",FACE,{"disambiguationData":[OSD([sQuery(id+"F0.wireOp",EDGE,"E12"),sQuery(id+"F0.wireOp",EDGE,"E13"),sQuery(id+"F0.wireOp",EDGE,"E14"),sQuery(id+"F0.wireOp",EDGE,"E15"),sQuery(id+"F0.wireOp",EDGE,"E17.filletArc"),sQuery(id+"F0.wireOp",EDGE,"E18.filletArc"),sQuery(id+"F0.wireOp",EDGE,"E19.filletArc"),sQuery(id+"F0.wireOp",EDGE,"E20.filletArc"),sQuery(id+"F0.wireOp",EDGE,"E25.0"),sQuery(id+"F0.wireOp",EDGE,"E25.1"),sQuery(id+"F0.wireOp",EDGE,"E25.2"),sQuery(id+"F0.wireOp",EDGE,"E25.3"),sQuery(id+"F0.wireOp",EDGE,"E25.4"),sQuery(id+"F0.wireOp",EDGE,"E25.5"),sQuery(id+"F0.wireOp",EDGE,"E25.6"),sQuery(id+"F0.wireOp",EDGE,"E25.7")])],"isStart":false});
            extrude(context, id + "F17", {"entities" : qUnion([Q0, Q1, Q2]), "endBound" : BoundingType.UP_TO_SURFACE, "endBoundEntityFace" : qUnion([Q3]), "depth" : mm});
        }
        {
            var Q0;
            Q0 = qSketchRegion(id + "F16", true);
            extrude(context, id + "F18", {"entities" : qUnion([Q0]), "operationType" : NewBodyOperationType.ADD, "depth" : 25 * mm});
        }
    });
